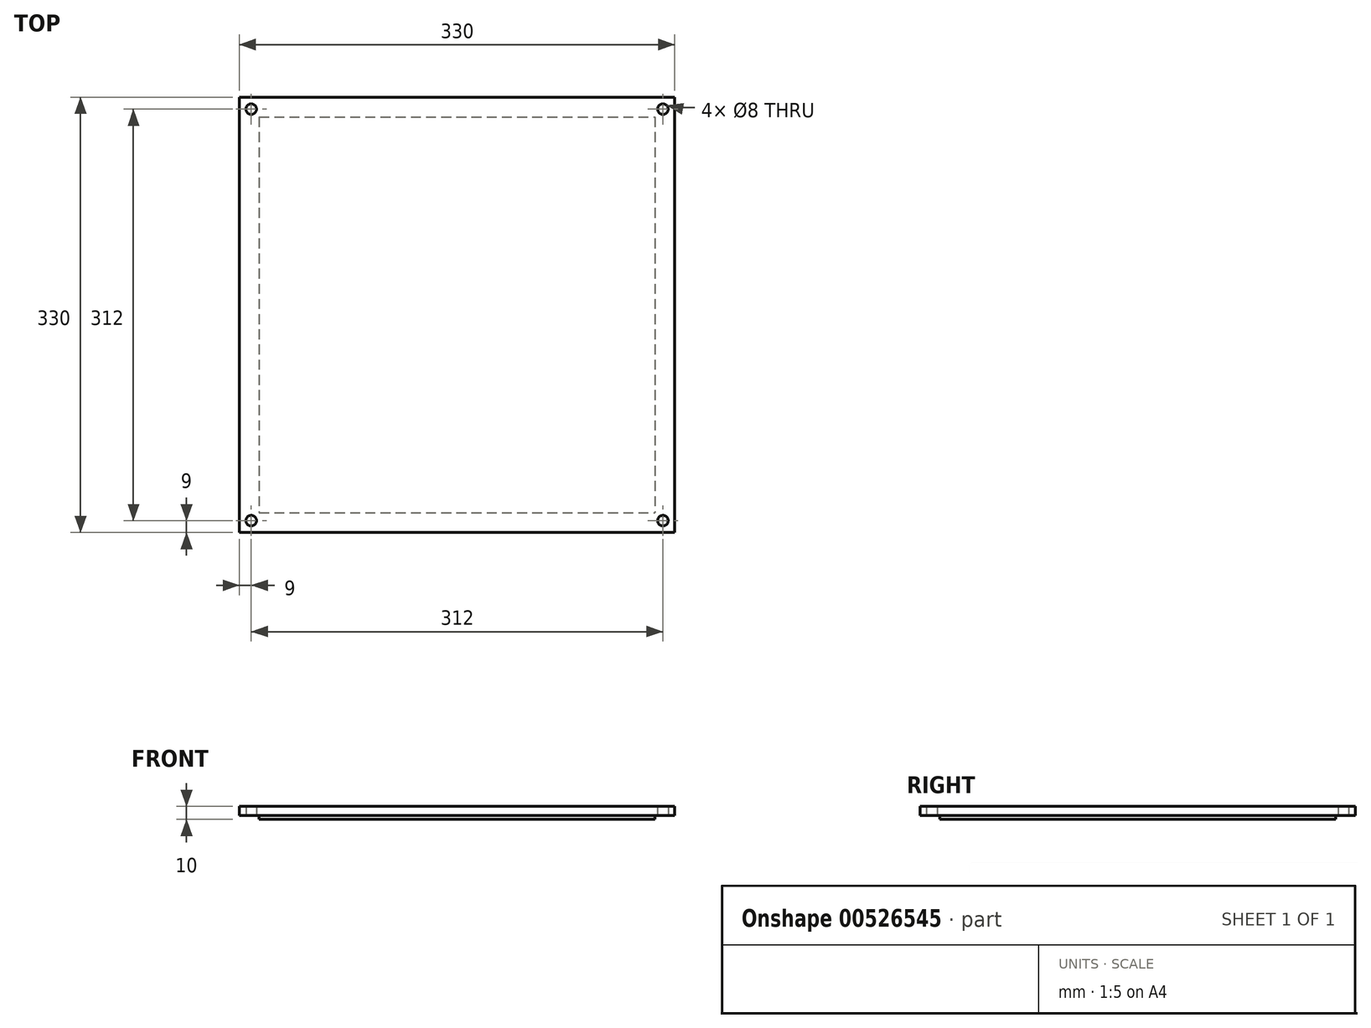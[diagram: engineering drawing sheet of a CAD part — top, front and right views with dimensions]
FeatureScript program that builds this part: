
annotation { "Feature Type Name" : "Feature", "Feature Type Description" : "" }
export const myFeature = defineFeature(function(context is Context, id is Id, definition is map)
    precondition{}
    {
        {
            var Q0;
            Q0=qCreatedBy(makeId("Top.planeOp"),FACE);
            var sketch = newSketch(context, id + "F0", { "sketchPlane" : qUnion([Q0])});
            skLineSegment(sketch, "E0.bottom", {"start": v(-150, 150) * mm, "end": v(150, 150) * mm});
            skLineSegment(sketch, "E0.top", {"start": v(-150, -150) * mm, "end": v(150, -150) * mm});
            skLineSegment(sketch, "E0.left", {"start": v(-150, 150) * mm, "end": v(-150, -150) * mm});
            skLineSegment(sketch, "E0.right", {"start": v(150, 150) * mm, "end": v(150, -150) * mm});
            skPoint(sketch, "E0.middle", {"position": v(0, 0) * mm});
            skLineSegment(sketch, "E1.left", {"start": v(-150, 150) * mm, "end": v(-150, 150) * mm});
            skLineSegment(sketch, "E1.right", {"start": v(150, 150) * mm, "end": v(150, 150) * mm});
            skLineSegment(sketch, "E2.bottom", {"start": v(-165, 165) * mm, "end": v(165, 165) * mm});
            skLineSegment(sketch, "E2.top", {"start": v(-165, -165) * mm, "end": v(165, -165) * mm});
            skLineSegment(sketch, "E2.left", {"start": v(-165, 165) * mm, "end": v(-165, -165) * mm});
            skLineSegment(sketch, "E2.right", {"start": v(165, 165) * mm, "end": v(165, -165) * mm});
            skSolve(sketch);
        }
        {
            var Q0;
            Q0=makeQuery(id+"F0.imprint","IMPRINT",FACE,{"disambiguationData":[TD([[makeQuery(id+"F0.imprint","IMPRINT",EDGE,{"derivedFrom":sQuery(id+"F0.wireOp",EDGE,"E0.top")}),-1.0]])]});
            var Q1;
            Q1=makeQuery(id+"F0.imprint","IMPRINT",FACE,{"disambiguationData":[TD([[makeQuery(id+"F0.imprint","IMPRINT",EDGE,{"derivedFrom":sQuery(id+"F0.wireOp",EDGE,"E0.top")}),1.0]])]});
            extrude(context, id + "F1", {"entities" : qUnion([Q0, Q1]), "depth" : 7 * mm, "offsetDistance" : 25 * mm});
        }
        {
            var Q0;
            Q0=makeQuery(id+"F0.imprint","IMPRINT",FACE,{"disambiguationData":[TD([[makeQuery(id+"F0.imprint","IMPRINT",EDGE,{"derivedFrom":sQuery(id+"F0.wireOp",EDGE,"E0.top")}),1.0]])]});
            extrude(context, id + "F2", {"entities" : qUnion([Q0]), "operationType" : NewBodyOperationType.ADD, "oppositeDirection" : true, "depth" : 3 * mm, "offsetDistance" : 25 * mm});
        }
        {
            var Q0;
            Q0=qCreatedBy(makeId("Top.planeOp"),FACE);
            var sketch = newSketch(context, id + "F3", { "sketchPlane" : qUnion([Q0])});
            skCircle(sketch, "E3", {"center": v(-156, 156) * mm, "radius": 4 * mm});
            skCircle(sketch, "E4.MirrorC", {"center": v(156, 156) * mm, "radius": 4 * mm});
            skCircle(sketch, "E5.MirrorC", {"center": v(156, -156) * mm, "radius": 4 * mm});
            skCircle(sketch, "E6.MirrorC", {"center": v(-156, -156) * mm, "radius": 4 * mm});
            skSolve(sketch);
        }
        {
            var Q0;
            Q0 = qSketchRegion(id + "F3", true);
            extrude(context, id + "F4", {"entities" : qUnion([Q0]), "operationType" : NewBodyOperationType.REMOVE, "depth" : 8 * mm, "offsetDistance" : 25 * mm});
        }
    });
